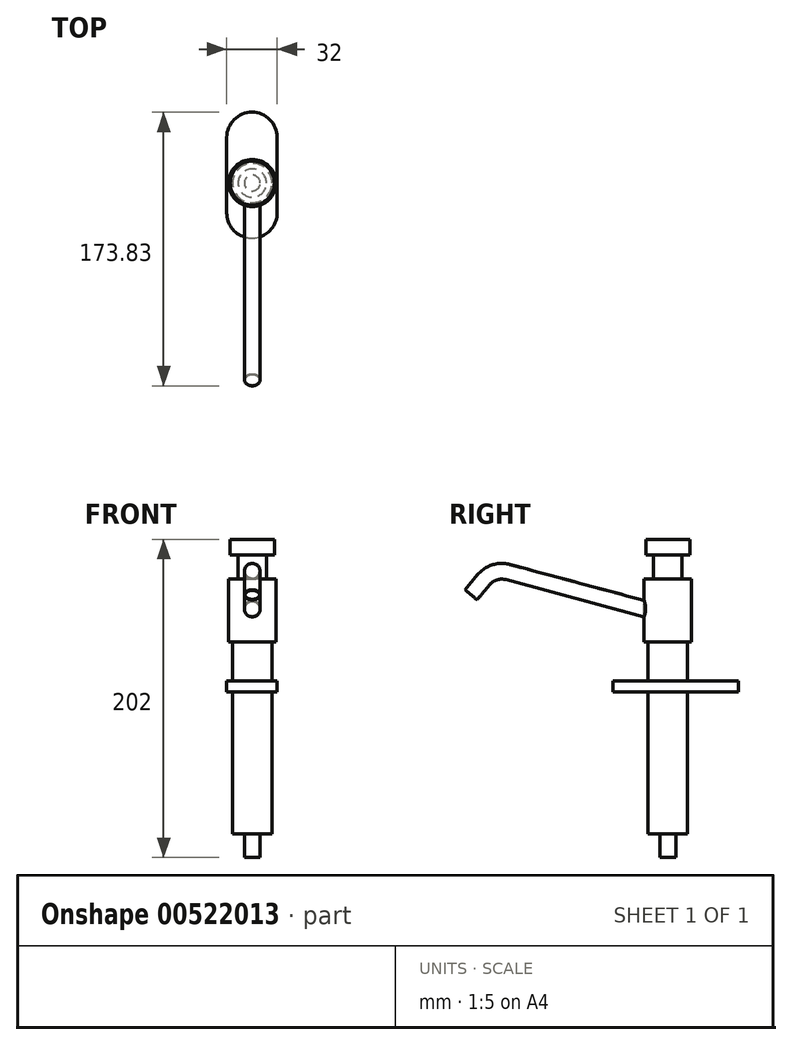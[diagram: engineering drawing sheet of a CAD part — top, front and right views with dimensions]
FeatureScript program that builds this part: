
annotation { "Feature Type Name" : "Feature", "Feature Type Description" : "" }
export const myFeature = defineFeature(function(context is Context, id is Id, definition is map)
    precondition{}
    {
        {
            var Q0;
            Q0=qCreatedBy(makeId("Top.planeOp"),FACE);
            var sketch = newSketch(context, id + "F0", { "sketchPlane" : qUnion([Q0])});
            skLineSegment(sketch, "E0", {"start": v(-16.21, 0) * mm, "end": v(-16.21, 48) * mm});
            skLineSegment(sketch, "E1", {"start": v(15.79, 0) * mm, "end": v(15.79, 48) * mm});
            skArc(sketch, "E2", {"start": v(15.79, 48) * mm, "mid": v(-0.21, 64) * mm, "end": v(-16.21, 48) * mm});
            skArc(sketch, "E3", {"start": v(-16.21, 0) * mm, "mid": v(-0.21, -16) * mm, "end": v(15.79, 0) * mm});
            skSolve(sketch);
        }
        {
            var Q0;
            Q0=makeQuery(id+"F0.imprint","IMPRINT",FACE,{"disambiguationData":[TD([[makeQuery(id+"F0.imprint","IMPRINT",EDGE,{"derivedFrom":sQuery(id+"F0.wireOp",EDGE,"E0")}),-1.0]])]});
            extrude(context, id + "F1", {"entities" : qUnion([Q0]), "depth" : 7 * mm, "offsetDistance" : 25 * mm});
        }
        {
            var Q0;
            Q0=qCreatedBy(makeId("Right.planeOp"),FACE);
            var sketch = newSketch(context, id + "F2", { "sketchPlane" : qUnion([Q0])});
            skLineSegment(sketch, "E4", {"start": v(19, 97) * mm, "end": v(19, -105) * mm});
            skLineSegment(sketch, "E5", {"start": v(19, 97) * mm, "end": v(33, 97) * mm});
            skLineSegment(sketch, "E6", {"start": v(33, 97) * mm, "end": v(33, 87) * mm});
            skLineSegment(sketch, "E7", {"start": v(33, 87) * mm, "end": v(28, 87) * mm});
            skLineSegment(sketch, "E8", {"start": v(28, 87) * mm, "end": v(28, 72) * mm});
            skLineSegment(sketch, "E9", {"start": v(28, 72) * mm, "end": v(34, 72) * mm});
            skLineSegment(sketch, "E10", {"start": v(34, 72) * mm, "end": v(34, 32) * mm});
            skLineSegment(sketch, "E11", {"start": v(34, 32) * mm, "end": v(31.5, 32) * mm});
            skLineSegment(sketch, "E12", {"start": v(31.5, 32) * mm, "end": v(31.5, -90) * mm});
            skLineSegment(sketch, "E13", {"start": v(31.5, -90) * mm, "end": v(24, -90) * mm});
            skLineSegment(sketch, "E14", {"start": v(24, -90) * mm, "end": v(24, -105) * mm});
            skLineSegment(sketch, "E15", {"start": v(24, -105) * mm, "end": v(19, -105) * mm});
            skSolve(sketch);
        }
        {
            var Q0;
            Q0=makeQuery(id+"F2.imprint","IMPRINT",FACE,{"disambiguationData":[TD([[makeQuery(id+"F2.imprint","IMPRINT",EDGE,{"derivedFrom":sQuery(id+"F2.wireOp",EDGE,"E4")}),1.0]])]});
            var Q1;
            Q1 = qConstructionFilter(qBodyType(qCreatedBy(id + "F2" ,EDGE), BodyType.WIRE), ConstructionObject.NO);
            var Q2;
            Q2=sQuery(id+"F2.wireOp",EDGE,"E4");
            revolve(context, id + "F3", {"operationType" : NewBodyOperationType.ADD, "entities" : qUnion([Q0]), "surfaceEntities" : qUnion([Q1]), "axis" : qUnion([Q2]), "revolveType" : RevolveType.FULL});
        }
        {
            var Q0;
            Q0=qCreatedBy(makeId("Right.planeOp"),FACE);
            var sketch = newSketch(context, id + "F4", { "sketchPlane" : qUnion([Q0])});
            skLineSegment(sketch, "E16", {"start": v(19, 49) * mm, "end": v(-82.58, 76.22) * mm});
            skLineSegment(sketch, "E17", {"start": v(-97.96, 71.37) * mm, "end": v(-106, 61.79) * mm});
            skPoint(sketch, "E18.visualSharp", {"position": v(-91.82, 78.7) * mm});
            skArc(sketch, "E18.filletArc", {"start": v(-82.58, 76.22) * mm, "mid": v(-90.98, 76.04) * mm, "end": v(-97.96, 71.37) * mm});
            skSolve(sketch);
        }
        {
            var Q0;
            Q0=sQuery(id+"F4.wireOp",VERTEX,"E17.end");
            var Q1;
            Q1=sQuery(id+"F4.wireOp",EDGE,"E17");
            cPlane(context, id + "F5", {"entities" : qUnion([Q0, Q1]), "cplaneType" : CPlaneType.LINE_POINT, "offset" : 25 * mm, "width" : 150 * mm, "height" : 150 * mm});
        }
        {
            var Q0;
            Q0=qCreatedBy(id+"F5.planeOp",FACE);
            var sketch = newSketch(context, id + "F6", { "sketchPlane" : qUnion([Q0])});
            skCircle(sketch, "E19", {"center": v(0, 120.92) * mm, "radius": 4.5 * mm});
            skCircle(sketch, "E20", {"center": v(0, 120.92) * mm, "radius": 5 * mm});
            skSolve(sketch);
        }
        {
            var Q0;
            Q0 = qSketchRegion(id + "F6", true);
            var Q1;
            Q1=sQuery(id+"F4.wireOp",EDGE,"E17");
            var Q2;
            Q2=sQuery(id+"F4.wireOp",EDGE,"E18.filletArc");
            var Q3;
            Q3=sQuery(id+"F4.wireOp",EDGE,"E16");
            sweep(context, id + "F7", {"operationType" : NewBodyOperationType.ADD, "profiles" : qUnion([Q0]), "path" : qUnion([Q1, Q2, Q3])});
        }
    });
